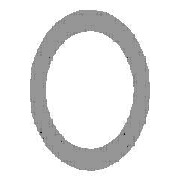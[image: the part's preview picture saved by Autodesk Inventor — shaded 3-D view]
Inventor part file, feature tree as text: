
AUTODESK INVENTOR PART (.ipt)
format: ipt  version: 2013 (Build 170138000, 138)  size: 113,664 bytes
history: native  units: mm (DEFAULTED — no unit token found)
features: other x4, sketch x3, plane x1
ambient origin geometry x8: Origin, YZ Plane, XZ Plane, XY Plane, X Axis, Y Axis, Z Axis, Center Point
bodies: Solid1 (feature_tree), Body (feature_tree)
feature tree (8):
  parser-record x1  (decoder bookkeeping rows leaked as tree rows — omitted from the tree; the rows remain in map.json)
  other  "Driven Length"
  other  "Start plane"
  other  "End plane"
  sketch  "Sketch"  dims[d2=101.6mm d3=0.0mm d4=-0.0mm d5=101.6mm d6=90.0deg d7=101.6mm]
  sketch  "Sketch3"  dims[d0=42.164mm]
  plane  "Work Plane3"
  sketch  "Sketch4"  dims[d1=3.556mm]
